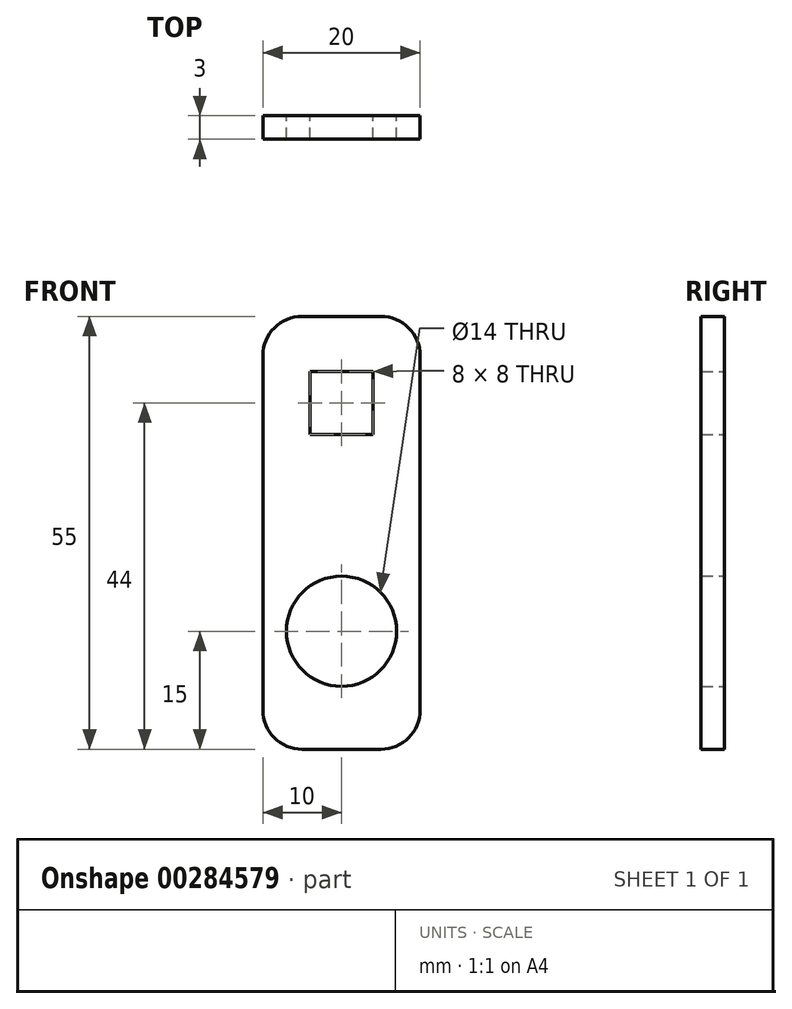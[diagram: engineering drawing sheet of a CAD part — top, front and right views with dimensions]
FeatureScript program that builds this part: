
annotation { "Feature Type Name" : "Feature", "Feature Type Description" : "" }
export const myFeature = defineFeature(function(context is Context, id is Id, definition is map)
    precondition{}
    {
        {
            var Q0;
            Q0=qCreatedBy(makeId("Front.planeOp"),FACE);
            var sketch = newSketch(context, id + "F0", { "sketchPlane" : qUnion([Q0])});
            skLineSegment(sketch, "E0.bottom", {"start": v(5, 25) * mm, "end": v(-5, 25) * mm});
            skLineSegment(sketch, "E0.top", {"start": v(5, -30) * mm, "end": v(-5, -30) * mm});
            skLineSegment(sketch, "E0.left", {"start": v(10, 20) * mm, "end": v(10, -25) * mm});
            skLineSegment(sketch, "E0.right", {"start": v(-10, 20) * mm, "end": v(-10, -25) * mm});
            skPoint(sketch, "E0.middle", {"position": v(0, 0) * mm});
            skPoint(sketch, "E1.visualSharp", {"position": v(-10, 25) * mm});
            skArc(sketch, "E1.filletArc", {"start": v(-5, 25) * mm, "mid": v(-8.54, 23.54) * mm, "end": v(-10, 20) * mm});
            skPoint(sketch, "E2.visualSharp", {"position": v(10, 25) * mm});
            skArc(sketch, "E2.filletArc", {"start": v(10, 20) * mm, "mid": v(8.54, 23.54) * mm, "end": v(5, 25) * mm});
            skPoint(sketch, "E3.visualSharp", {"position": v(-10, -30) * mm});
            skArc(sketch, "E3.filletArc", {"start": v(-10, -25) * mm, "mid": v(-8.54, -28.54) * mm, "end": v(-5, -30) * mm});
            skPoint(sketch, "E4.visualSharp", {"position": v(10, -30) * mm});
            skArc(sketch, "E4.filletArc", {"start": v(5, -30) * mm, "mid": v(8.54, -28.54) * mm, "end": v(10, -25) * mm});
            skLineSegment(sketch, "E5.bottom", {"start": v(4, 10) * mm, "end": v(-4, 10) * mm, "construction": true});
            skLineSegment(sketch, "E5.top", {"start": v(4, 18) * mm, "end": v(-4, 18) * mm, "construction": true});
            skLineSegment(sketch, "E5.left", {"start": v(4, 10) * mm, "end": v(4, 18) * mm});
            skLineSegment(sketch, "E5.right", {"start": v(-4, 10) * mm, "end": v(-4, 18) * mm});
            skCircle(sketch, "E6", {"center": v(0, -15) * mm, "radius": 7 * mm});
            skLineSegment(sketch, "E7", {"start": v(-4, 18) * mm, "end": v(4, 18) * mm});
            skLineSegment(sketch, "E8", {"start": v(-4, 10) * mm, "end": v(4, 10) * mm});
            skPoint(sketch, "E9", {"position": v(0, 14) * mm});
            skSolve(sketch);
        }
        {
            var Q0;
            Q0=qSketchRegion(id+"F0",true);
            extrude(context, id + "F1", {"entities" : qUnion([Q0]), "depth" : 3 * mm});
        }
    });
